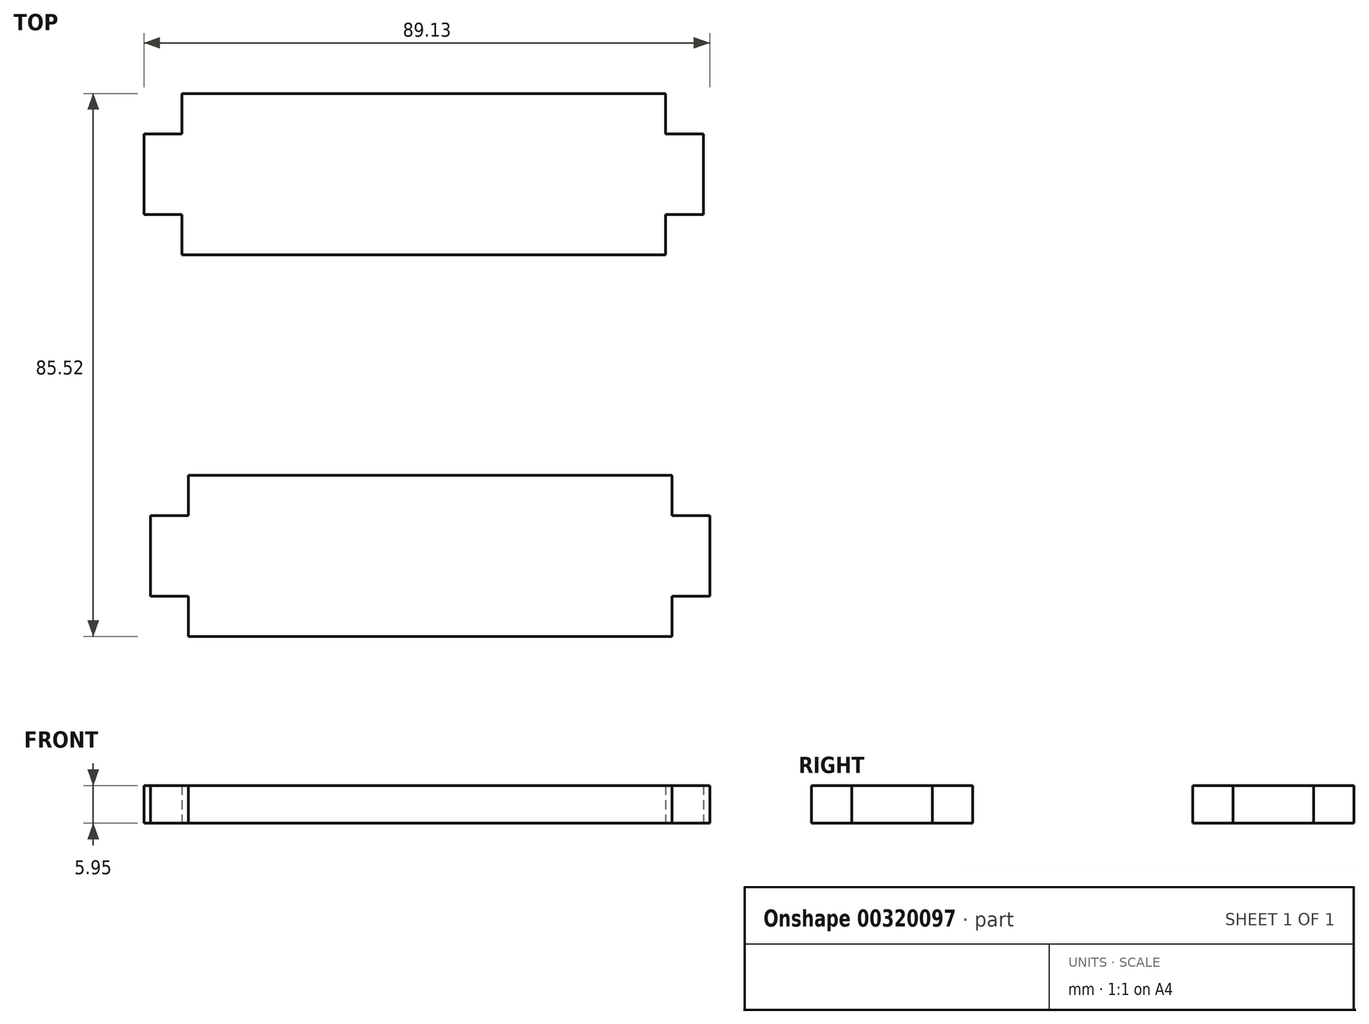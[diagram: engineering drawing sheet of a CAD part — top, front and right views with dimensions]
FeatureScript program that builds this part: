
annotation { "Feature Type Name" : "Feature", "Feature Type Description" : "" }
export const myFeature = defineFeature(function(context is Context, id is Id, definition is map)
    precondition{}
    {
        {
            var Q0;
            Q0=qCreatedBy(makeId("Top.planeOp"),FACE);
            var sketch = newSketch(context, id + "F0", { "sketchPlane" : qUnion([Q0])});
            skLineSegment(sketch, "E0.bottom", {"start": v(-39.07, 43.12) * mm, "end": v(37.13, 43.12) * mm});
            skLineSegment(sketch, "E0.top", {"start": v(-39.07, 17.72) * mm, "end": v(37.13, 17.72) * mm});
            skLineSegment(sketch, "E0.left", {"start": v(-39.07, 43.12) * mm, "end": v(-39.07, 17.72) * mm});
            skLineSegment(sketch, "E0.right", {"start": v(37.13, 43.12) * mm, "end": v(37.13, 17.72) * mm});
            skLineSegment(sketch, "E1.bottom", {"start": v(-38.06, -17) * mm, "end": v(38.14, -17) * mm});
            skLineSegment(sketch, "E1.top", {"start": v(-38.06, -42.4) * mm, "end": v(38.14, -42.4) * mm});
            skLineSegment(sketch, "E1.left", {"start": v(-38.06, -17) * mm, "end": v(-38.06, -42.4) * mm});
            skLineSegment(sketch, "E1.right", {"start": v(38.14, -17) * mm, "end": v(38.14, -42.4) * mm});
            skLineSegment(sketch, "E2.bottom", {"start": v(-13.67, 43.12) * mm, "end": v(11.73, 43.12) * mm});
            skLineSegment(sketch, "E2.top", {"start": v(-13.67, 49.07) * mm, "end": v(11.73, 49.07) * mm});
            skLineSegment(sketch, "E2.left", {"start": v(-13.67, 43.12) * mm, "end": v(-13.67, 49.07) * mm});
            skLineSegment(sketch, "E2.right", {"start": v(11.73, 43.12) * mm, "end": v(11.73, 49.07) * mm});
            skLineSegment(sketch, "E3.bottom", {"start": v(-39.07, 24.07) * mm, "end": v(-45.03, 24.07) * mm});
            skLineSegment(sketch, "E3.top", {"start": v(-39.07, 36.77) * mm, "end": v(-45.03, 36.77) * mm});
            skLineSegment(sketch, "E3.left", {"start": v(-39.07, 24.07) * mm, "end": v(-39.07, 36.77) * mm});
            skLineSegment(sketch, "E3.right", {"start": v(-45.03, 24.07) * mm, "end": v(-45.03, 36.77) * mm});
            skLineSegment(sketch, "E4.bottom", {"start": v(37.13, 36.77) * mm, "end": v(43.08, 36.77) * mm});
            skLineSegment(sketch, "E4.top", {"start": v(37.13, 24.07) * mm, "end": v(43.08, 24.07) * mm});
            skLineSegment(sketch, "E4.left", {"start": v(37.13, 36.77) * mm, "end": v(37.13, 24.07) * mm});
            skLineSegment(sketch, "E4.right", {"start": v(43.08, 36.77) * mm, "end": v(43.08, 24.07) * mm});
            skLineSegment(sketch, "E5.bottom", {"start": v(38.14, -36.05) * mm, "end": v(44.1, -36.05) * mm});
            skLineSegment(sketch, "E5.top", {"start": v(38.14, -23.35) * mm, "end": v(44.1, -23.35) * mm});
            skLineSegment(sketch, "E5.left", {"start": v(38.14, -36.05) * mm, "end": v(38.14, -23.35) * mm});
            skLineSegment(sketch, "E5.right", {"start": v(44.1, -36.05) * mm, "end": v(44.1, -23.35) * mm});
            skLineSegment(sketch, "E6.bottom", {"start": v(-38.06, -23.35) * mm, "end": v(-44, -23.35) * mm});
            skLineSegment(sketch, "E6.top", {"start": v(-38.06, -36.05) * mm, "end": v(-44, -36.05) * mm});
            skLineSegment(sketch, "E6.left", {"start": v(-38.06, -23.35) * mm, "end": v(-38.06, -36.05) * mm});
            skLineSegment(sketch, "E6.right", {"start": v(-44, -23.35) * mm, "end": v(-44, -36.05) * mm});
            skSolve(sketch);
        }
        {
            var Q0;
            {var subQ4=sQuery(id+"F0.wireOp",EDGE,"E0.top");Q0=makeQuery(id+"F0.imprint","IMPRINT",FACE,{"disambiguationData":[TD([[makeQuery(id+"F0.imprint","IMPRINT",EDGE,{"derivedFrom":subQ4}),1.0]])]});}
            var Q1;
            Q1=makeQuery(id+"F0.imprint","IMPRINT",FACE,{"disambiguationData":[TD([[makeQuery(id+"F0.imprint","IMPRINT",EDGE,{"derivedFrom":sQuery(id+"F0.wireOp",EDGE,"E3.bottom")}),-1.0]])]});
            var Q2;
            Q2=makeQuery(id+"F0.imprint","IMPRINT",FACE,{"disambiguationData":[TD([[makeQuery(id+"F0.imprint","IMPRINT",EDGE,{"derivedFrom":sQuery(id+"F0.wireOp",EDGE,"E2.bottom")}),1.0]])]});
            var Q3;
            Q3=makeQuery(id+"F0.imprint","IMPRINT",FACE,{"disambiguationData":[TD([[makeQuery(id+"F0.imprint","IMPRINT",EDGE,{"derivedFrom":sQuery(id+"F0.wireOp",EDGE,"E4.bottom")}),-1.0]])]});
            var Q4;
            {var subQ3=sQuery(id+"F0.wireOp",EDGE,"E1.bottom");Q4=makeQuery(id+"F0.imprint","IMPRINT",FACE,{"disambiguationData":[TD([[makeQuery(id+"F0.imprint","IMPRINT",EDGE,{"derivedFrom":subQ3}),-1.0]])]});}
            var Q5;
            Q5=makeQuery(id+"F0.imprint","IMPRINT",FACE,{"disambiguationData":[TD([[makeQuery(id+"F0.imprint","IMPRINT",EDGE,{"derivedFrom":sQuery(id+"F0.wireOp",EDGE,"E6.bottom")}),1.0]])]});
            var Q6;
            Q6=makeQuery(id+"F0.imprint","IMPRINT",FACE,{"disambiguationData":[TD([[makeQuery(id+"F0.imprint","IMPRINT",EDGE,{"derivedFrom":sQuery(id+"F0.wireOp",EDGE,"E5.bottom")}),1.0]])]});
            extrude(context, id + "F1", {"entities" : qUnion([Q0, Q1, Q2, Q3, Q4, Q5, Q6]), "depth" : 5.95 * mm});
        }
    });
